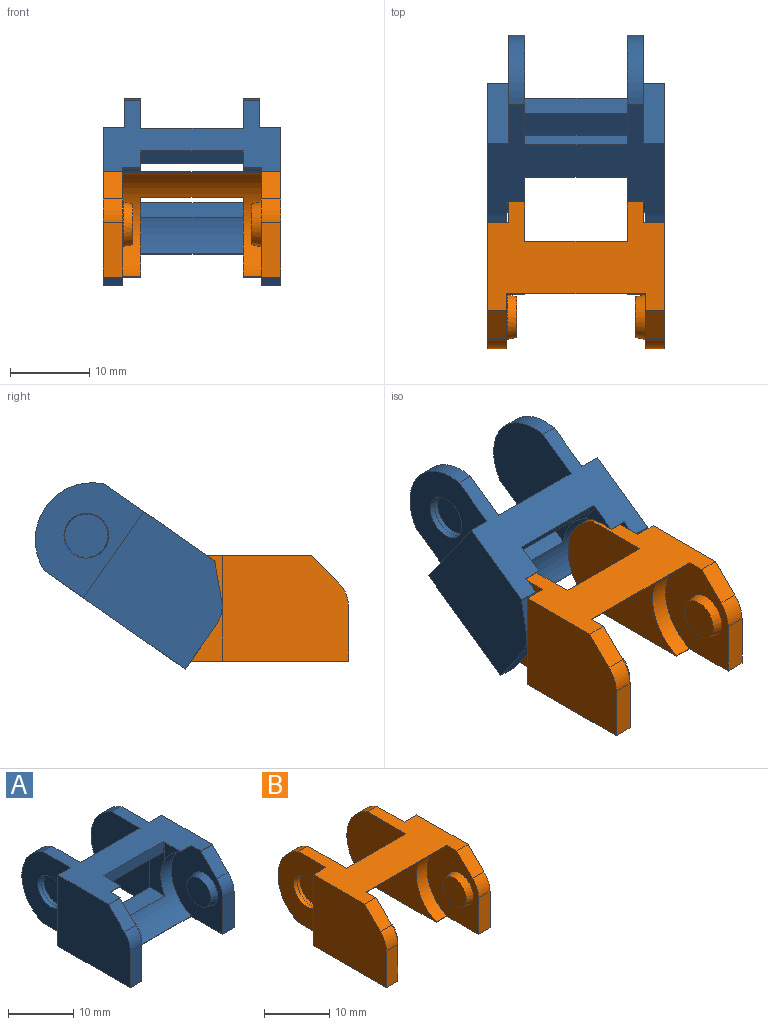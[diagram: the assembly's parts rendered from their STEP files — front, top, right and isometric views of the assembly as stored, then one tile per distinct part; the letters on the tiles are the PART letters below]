
ASSEMBLY  parts=2 mates=1
PART A: 56 faces, bbox 22.4x26.2x13.3 mm
  f0: plane 13.3x12.74mm, normal (-1,0,0), area 148.8mm2, adj f2,f3,f8,f34,f41,f53,f54
  f1: plane 13.3x12.74mm, normal (1,0,0), area 148.8mm2, adj f2,f3,f8,f33,f40,f53,f54
  f2: plane 22.44x21.72mm, normal (0,0,-1), area 228.5mm2, adj f0,f1,f4,f5,f6,f7,f8,f12
  f3: plane 22.44x17.07mm, normal (0,0,1), area 184.6mm2, adj f0,f1,f4,f6,f7,f12,f13,f14
  f4: plane 13.3x11.08mm, normal (-1,0,0), area 93.4mm2, adj f2,f3,f5,f12,f16,f47,f48,f49
  f5: cylinder r=7.2mm len=1.12mm, axis (-1,0,0), area 0mm2, adj f2,f4,f22,f50
  f6: plane 15.67x13.3mm, normal (1,0,0), area 196.6mm2, adj f2,f3,f47,f48,f49,f50,f52
  f7: plane 13.3x11.08mm, normal (1,0,0), area 93.7mm2, adj f2,f3,f12,f29,f30,f43,f44,f45
  f8: plane 12.89x3.28mm, normal (0,1,0), area 42.3mm2, adj f0,f1,f2,f42
  f9: plane 12.7x0.01mm, normal (0,-1,0), area 0.1mm2, adj f10,f11,f12,f42
  f10: cone r=7.2mm half-angle=87.6deg, axis (1,0,0), area 0mm2, adj f9,f12,f42
  f11: cone r=7.2mm half-angle=87.6deg, axis (-1,0,0), area 0mm2, adj f9,f12,f42
  f12: cylinder r=7.2mm len=17.49mm, axis (-1,0,0), area 138.2mm2, adj f2,f3,f4,f7,f9,f10,f11,f18
  f13: plane 13.3x10.49mm, normal (1,0,0), area 94.9mm2, adj f2,f3,f34,f39,f52
  f14: plane 13.3x10.49mm, normal (-1,0,0), area 98mm2, adj f2,f3,f33,f37,f51
  f15: plane 5.13x5.13mm, normal (-1,0,0), area 20.7mm2, adj f16
  f16: cone r=2.56mm half-angle=12.7deg, axis (1,0,0), area 22.1mm2, adj f4,f15
  f17: plane 15.67x13.3mm, normal (-1,0,0), area 196.6mm2, adj f2,f3,f43,f44,f45,f46,f51
  f18: plane 0.16x0.07mm, normal (-1,0,0), area 0mm2, adj f3,f12,f19
  f19: plane 2.29x0.07mm, normal (0,-1,0), area 0.2mm2, adj f3,f12,f18,f20
  f20: plane 3.44x3.27mm, normal (-1,0,0), area 4.5mm2, adj f3,f12,f19,f41
  f21: plane 0.16x0.07mm, normal (-1,0,0), area 0mm2, adj f2,f12,f23
  f22: plane 1.12x0.58mm, normal (-1,0,0), area 0.3mm2, adj f2,f5,f50
  f23: plane 17.46x0.07mm, normal (0,-1,0), area 1.2mm2, adj f2,f12,f21,f27
  f24: plane 3.44x3.27mm, normal (1,0,0), area 4.5mm2, adj f3,f12,f25,f40
  f25: plane 2.29x0.07mm, normal (0,-1,0), area 0.2mm2, adj f3,f12,f24,f28
  f26: plane 1.12x0.58mm, normal (1,0,0), area 0.3mm2, adj f2,f29,f43
  f27: plane 0.16x0.07mm, normal (1,0,0), area 0mm2, adj f2,f12,f23
  f28: plane 0.16x0.07mm, normal (1,0,0), area 0mm2, adj f3,f12,f25
  f29: cylinder r=7.2mm len=1.12mm, axis (-1,0,0), area 0mm2, adj f2,f7,f26,f43
  f30: cylinder r=2.83mm len=5.66mm, axis (-1,0,0), area 1.6mm2, adj f7,f32
  f31: plane 5.13x5.13mm, normal (1,0,0), area 20.7mm2, adj f32
  f32: cone r=2.56mm half-angle=12.7deg, axis (-1,0,0), area 20.4mm2, adj f30,f31
  f33: cylinder r=7.2mm len=13.3mm, axis (1,0,0), area 34.7mm2, adj f1,f2,f3,f14
  f34: cylinder r=7.2mm len=13.3mm, axis (1,0,0), area 34.7mm2, adj f0,f2,f3,f13
  f35: plane 5.45x5.45mm, normal (-1,0,0), area 23.3mm2, adj f36
  f36: cone r=2.76mm half-angle=12.7deg, axis (-1,0,0), area 8.3mm2, adj f35,f37
  f37: cylinder r=2.83mm len=5.66mm, axis (-1,0,0), area 13.3mm2, adj f14,f36
  f38: plane 5.45x5.45mm, normal (1,0,0), area 23.3mm2, adj f39
  f39: cone r=2.76mm half-angle=12.7deg, axis (1,0,0), area 22.4mm2, adj f13,f38
  f40: plane 10.02x3.18mm, normal (1,0,0), area 22.3mm2, adj f1,f3,f12,f24,f42,f54,f55
  f41: plane 10.02x3.18mm, normal (-1,0,0), area 22.3mm2, adj f0,f3,f12,f20,f42,f54,f55
  f42: plane 12.89x3.18mm, normal (0,0,1), area 41mm2, adj f8,f9,f10,f11,f12,f40,f41
  f43: plane 6.88x2.49mm, normal (0,-1,0), area 17mm2, adj f2,f7,f17,f26,f29,f46
  f44: plane 2.47x0.07mm, normal (0,-0.71,-0.71), area 0.2mm2, adj f3,f7,f17,f45
  f45: plane 3.44x3.43mm, normal (0,-0.71,0.71), area 12mm2, adj f7,f17,f44,f46
  f46: cylinder r=4.03mm len=2.92mm, axis (-1,0,0), area 8.1mm2, adj f7,f17,f43,f45
  f47: plane 2.47x0.07mm, normal (0,-0.71,-0.71), area 0.2mm2, adj f3,f4,f6,f48
  f48: plane 3.44x3.43mm, normal (0,-0.71,0.71), area 12mm2, adj f4,f6,f47,f49
  f49: cylinder r=4.03mm len=2.92mm, axis (-1,0,0), area 8.1mm2, adj f4,f6,f48,f50
  f50: plane 6.88x2.49mm, normal (0,-1,0), area 17mm2, adj f2,f4,f5,f6,f22,f49
  f51: plane 13.3x2.73mm, normal (0,1,0), area 36.3mm2, adj f2,f3,f14,f17
  f52: plane 13.3x2.73mm, normal (0,1,0), area 36.3mm2, adj f2,f3,f6,f13
  f53: plane 12.89x2mm, normal (0,1,0), area 25.8mm2, adj f0,f1,f3,f54
  f54: plane 12.89x5mm, normal (0,0,-1), area 64.5mm2, adj f0,f1,f40,f41,f53,f55
  f55: plane 12.89x2mm, normal (0,-1,0), area 25.8mm2, adj f3,f40,f41,f54
PART B: 39 faces, bbox 22.4x26.3x13.3 mm
  f0: plane 21.82x4.77mm, normal (0,0,-1), area 72.1mm2, adj f1,f7,f8,f15,f17,f23,f27,f31
  f1: plane 6.88x2.47mm, normal (0,-1,0), area 17mm2, adj f0,f17,f19,f27
  f2: plane 21.82x4.77mm, normal (0,0,-1), area 72.1mm2, adj f4,f5,f6,f12,f13,f16,f26,f32
  f3: cylinder r=7.2mm len=17.49mm, axis (-1,0,0), area 137.7mm2, adj f4,f6,f7,f9,f12,f22,f23,f24
  f4: plane 2.3x0.07mm, normal (0,-1,0), area 0.2mm2, adj f2,f3,f6,f12
  f5: plane 13.3x10.39mm, normal (1,0,0), area 93.6mm2, adj f2,f9,f13,f32,f37
  f6: plane 19.36x13.3mm, normal (-1,0,0), area 185.8mm2, adj f2,f3,f4,f9,f14,f32,f38
  f7: plane 19.36x13.3mm, normal (1,0,0), area 185.8mm2, adj f0,f3,f9,f14,f23,f31,f38
  f8: plane 13.3x10.39mm, normal (-1,0,0), area 96.7mm2, adj f0,f9,f15,f31,f35
  f9: plane 22.44x17.07mm, normal (0,0,1), area 206mm2, adj f3,f5,f6,f7,f8,f12,f13,f14
  f10: plane 5.13x5.13mm, normal (-1,0,0), area 20.7mm2, adj f11
  f11: cone r=2.56mm half-angle=12.7deg, axis (1,0,0), area 22.1mm2, adj f10,f12
  f12: plane 13.3x11.18mm, normal (-1,0,0), area 95.2mm2, adj f2,f3,f4,f9,f11,f20,f21,f26
  f13: plane 13.3x2.73mm, normal (0,1,0), area 36.3mm2, adj f2,f5,f9,f16
  f14: plane 12.89x3.24mm, normal (0,1,0), area 41.8mm2, adj f6,f7,f9,f38
  f15: plane 13.3x2.73mm, normal (0,1,0), area 36.3mm2, adj f0,f8,f9,f17
  f16: plane 15.87x13.3mm, normal (1,0,0), area 199.5mm2, adj f2,f9,f13,f20,f21,f26
  f17: plane 15.87x13.3mm, normal (-1,0,0), area 199.5mm2, adj f0,f1,f9,f15,f18,f19
  f18: plane 3.44x3.43mm, normal (0,-0.71,0.71), area 12mm2, adj f9,f17,f19,f27
  f19: cylinder r=4.13mm len=2.99mm, axis (-1,0,0), area 8.3mm2, adj f1,f17,f18,f27
  f20: plane 3.44x3.43mm, normal (0,-0.71,0.71), area 12mm2, adj f9,f12,f16,f21
  f21: cylinder r=4.13mm len=2.99mm, axis (-1,0,0), area 8.3mm2, adj f12,f16,f20,f26
  f22: plane 0.16x0.07mm, normal (-1,0,0), area 0mm2, adj f3,f9,f24
  f23: plane 2.3x0.07mm, normal (0,-1,0), area 0.2mm2, adj f0,f3,f7,f27
  f24: plane 17.46x0.07mm, normal (0,-1,0), area 1.2mm2, adj f3,f9,f22,f25
  f25: plane 0.16x0.07mm, normal (1,0,0), area 0mm2, adj f3,f9,f24
  f26: plane 6.88x2.47mm, normal (0,-1,0), area 17mm2, adj f2,f12,f16,f21
  f27: plane 13.3x11.18mm, normal (1,0,0), area 95.5mm2, adj f0,f1,f3,f9,f18,f19,f23,f28
  f28: cylinder r=2.83mm len=5.66mm, axis (-1,0,0), area 1.6mm2, adj f27,f30
  f29: plane 5.13x5.13mm, normal (1,0,0), area 20.7mm2, adj f30
  f30: cone r=2.56mm half-angle=12.7deg, axis (-1,0,0), area 20.4mm2, adj f28,f29
  f31: cylinder r=7.2mm len=13.3mm, axis (1,0,0), area 34.7mm2, adj f0,f7,f8,f9
  f32: cylinder r=7.2mm len=13.3mm, axis (1,0,0), area 34.7mm2, adj f2,f5,f6,f9
  f33: plane 5.45x5.45mm, normal (-1,0,0), area 23.3mm2, adj f34
  f34: cone r=2.76mm half-angle=12.7deg, axis (-1,0,0), area 8.3mm2, adj f33,f35
  f35: cylinder r=2.83mm len=5.66mm, axis (-1,0,0), area 13.3mm2, adj f8,f34
  f36: plane 5.45x5.45mm, normal (1,0,0), area 23.3mm2, adj f37
  f37: cone r=2.76mm half-angle=12.7deg, axis (1,0,0), area 22.4mm2, adj f5,f36
  f38: plane 12.89x3.2mm, normal (0,0,-1), area 41.2mm2, adj f3,f6,f7,f14
PLACE A rot(axis=(1,0,0),35deg) t=(-0.39,15.04,7.64)mm
PLACE B t=(-0.39,0.7,2.39)mm fixed
MATE revolute A.f5 <-> B.f34  axis (-1,0,0) through (7.09,7.54,2.39)mm
